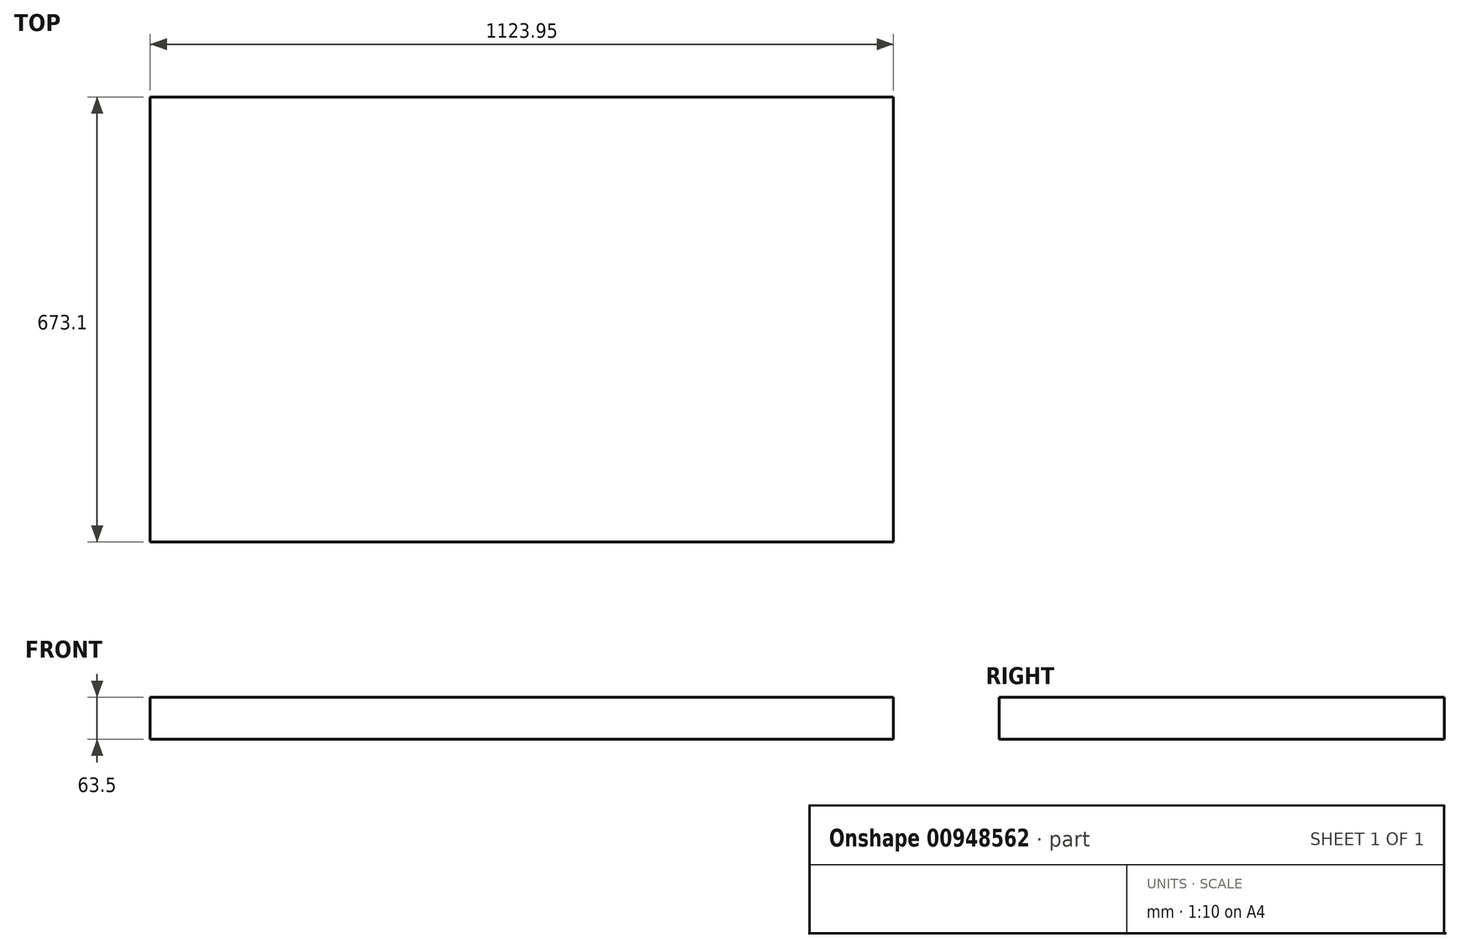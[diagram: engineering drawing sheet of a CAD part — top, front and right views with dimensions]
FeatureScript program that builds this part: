
annotation { "Feature Type Name" : "Feature", "Feature Type Description" : "" }
export const myFeature = defineFeature(function(context is Context, id is Id, definition is map)
    precondition{}
    {
        {
            var Q0;
            Q0=qCreatedBy(makeId("Top.planeOp"),FACE);
            var sketch = newSketch(context, id + "F0", { "sketchPlane" : qUnion([Q0])});
            skLineSegment(sketch, "E0.bottom", {"start": v(578.47, 336.55) * mm, "end": v(-545.48, 336.55) * mm});
            skLineSegment(sketch, "E0.top", {"start": v(578.47, -336.55) * mm, "end": v(-545.48, -336.55) * mm});
            skLineSegment(sketch, "E0.left", {"start": v(578.47, 336.55) * mm, "end": v(578.47, -336.55) * mm});
            skLineSegment(sketch, "E0.right", {"start": v(-545.48, 336.55) * mm, "end": v(-545.48, -336.55) * mm});
            skPoint(sketch, "E0.middle", {"position": v(16.5, 0) * mm});
            skSolve(sketch);
        }
        {
            var Q0;
            Q0 = qSketchRegion(id + "F0", true);
            extrude(context, id + "F1", {"entities" : qUnion([Q0]), "depth" : 63.5 * mm, "offsetDistance" : 25 * mm});
        }
    });
